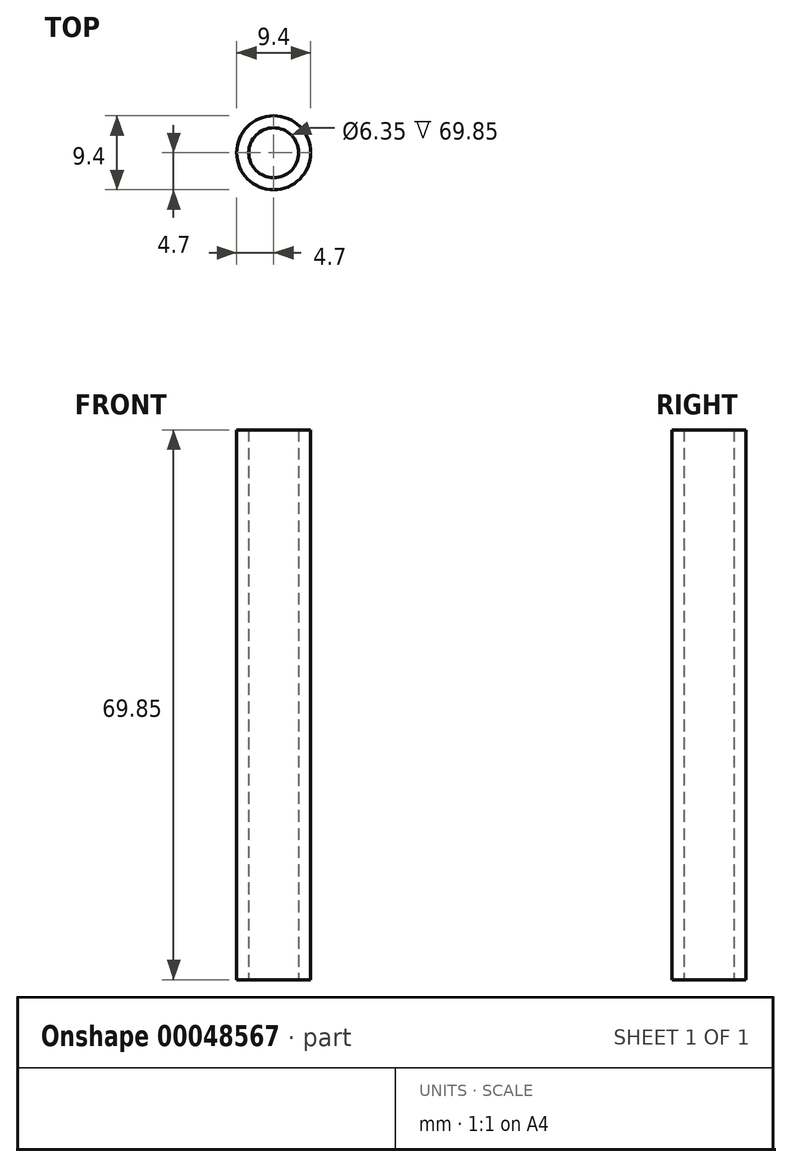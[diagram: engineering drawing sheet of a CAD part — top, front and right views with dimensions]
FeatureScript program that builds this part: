
annotation { "Feature Type Name" : "Feature", "Feature Type Description" : "" }
export const myFeature = defineFeature(function(context is Context, id is Id, definition is map)
    precondition{}
    {
        {
            var Q0;
            Q0=qCreatedBy(makeId("Top.planeOp"),FACE);
            var sketch = newSketch(context, id + "F0", { "sketchPlane" : qUnion([Q0])});
            skCircle(sketch, "E0", {"center": v(0, 0) * mm, "radius": 4.7 * mm});
            skCircle(sketch, "E1", {"center": v(0, 0) * mm, "radius": 3.18 * mm});
            skSolve(sketch);
        }
        {
            var Q0;
            Q0 = qSketchRegion(id + "F0", true);
            extrude(context, id + "F1", {"entities" : qUnion([Q0]), "depth" : 69.85 * mm});
        }
    });
